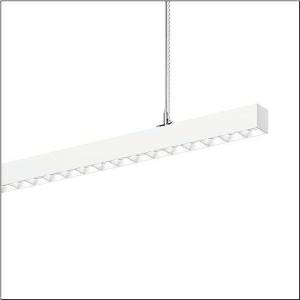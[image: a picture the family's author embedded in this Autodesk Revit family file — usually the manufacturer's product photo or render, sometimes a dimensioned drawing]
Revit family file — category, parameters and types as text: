
# Revit family: silica_r__21_51mx36da37wb_45fb
name_source: partatom
category: Lighting Fixtures
units: mm (PartAtom-declared; Revit-internal decimal feet)

## family parameters
Cut with Voids When Loaded = No
Host = Face
Light Source = No
Part Type = Normal
Room Calculation Point = No
Round Connector Dimension = Use Diameter
Shared = No

## types (1)
- --- (1 x LED, 7060 lm, 43 W, 3000K)
    Apparent Load = 43 VA
    CIE Flux Codes = 83 98 100 61 100
    Color Rendering = 80
    Color Temperature = 3000K
    Default Elevation = 1800 mm
    Description = Silica® 21, office luminaire, primary light control with darklight reflector, of PMMA, white, CAT 2 (L<= 3000cd/m²), light emission: direct/indirect distribution, primary light characteristic: symmetric, installation type: suspended mounting, LED, rated luminous flux: 7.060lm, luminous efficacy: 164lm/W, light colour: 830, colour temperature: 3000K, with terminal, 3+2-pole, max. 2.5mm², mains connection: 220..240V, AC, 50/60Hz, rated input power: 43W, luminaire housing, of aluminium, traffic white (RAL 9016), length: 1.204mm, width: 53mm, height: 53mm, protection rating (complete): IP20, insulation class (complete): insulation class I (protective earthing), certification: CE, permissible operating ambient temperature: 0..+35°C, standard: EN 50419, packaging unit: 1 piece
    Height = 53 mm
    Lamp = 1 x LED
    Lamp Light Flux = 7060 lm
    Lamp Power = 43 W
    Lamp count = 1
    Length = 1204 mm
    Luminous efficacy = 164 lm/W
    Manufacturer = Siteco
    ModVariant = No
    Model = 51MX36DA37WB
    Mounting Place = Ceiling
    Mounting Type = Pendant
    Number of Poles = 1
    OnlyDefault = Yes
    Power Factor = 1
    Product Name = Silica® 21
    Product group = office luminaire | ceiling pendant
    ProductGroupID = 905
    Protection Class = Protection class I
    Protection Degree = IP 20
    RLX_Detail_Level = 1
    RlxData = <blob elided: 40929 chars, md5=b0179ea7>
    Socket = socket
    Standby Power = 0 W
    System Light Flux = 7060 lm
    System Power = 43 W
    Type Comments = factory setting: luminous flux: 100 % | dim-lin: 254 | 359 mA
    Type Image = l_1251641.jpg
    URL = http://relux.com
    VarID = @adj_030413
    Voltage = 0 V
    Weight = 0.00 kg
    Width = 53 mm

## geometry (parser evidence)
native form markers: Blend x4, Sweep x13
no freeform markers — native parametric forms only
